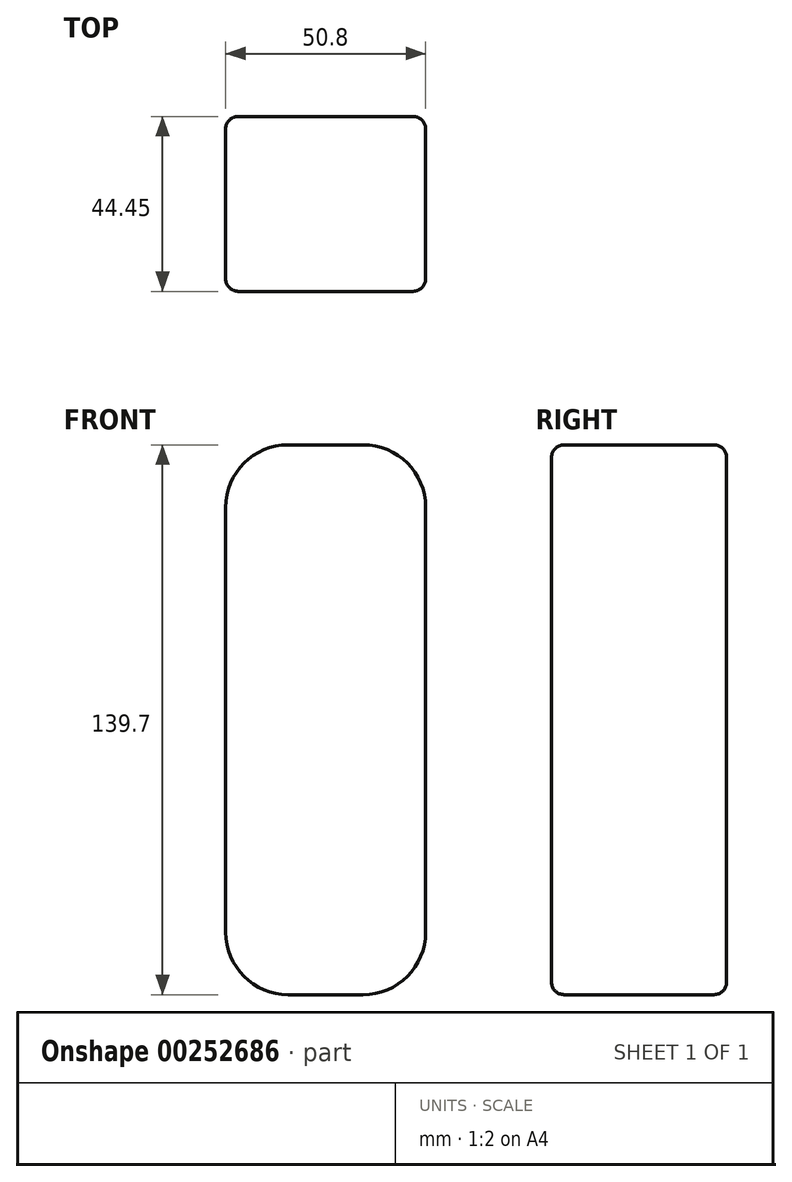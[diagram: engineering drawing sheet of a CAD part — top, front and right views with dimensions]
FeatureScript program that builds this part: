
annotation { "Feature Type Name" : "Feature", "Feature Type Description" : "" }
export const myFeature = defineFeature(function(context is Context, id is Id, definition is map)
    precondition{}
    {
        {
            var Q0;
            Q0=qCreatedBy(makeId("Front.planeOp"),FACE);
            var sketch = newSketch(context, id + "F0", { "sketchPlane" : qUnion([Q0])});
            skLineSegment(sketch, "E0.bottom", {"start": v(9.53, 69.85) * mm, "end": v(-9.53, 69.85) * mm});
            skLineSegment(sketch, "E0.top", {"start": v(9.52, -69.85) * mm, "end": v(-9.53, -69.85) * mm});
            skLineSegment(sketch, "E0.left", {"start": v(25.4, 53.98) * mm, "end": v(25.4, -53.98) * mm});
            skLineSegment(sketch, "E0.right", {"start": v(-25.4, 53.98) * mm, "end": v(-25.4, -53.98) * mm});
            skPoint(sketch, "E0.middle", {"position": v(0, 0) * mm});
            skPoint(sketch, "E1.visualSharp", {"position": v(-25.4, 69.85) * mm});
            skArc(sketch, "E1.filletArc", {"start": v(-9.53, 69.85) * mm, "mid": v(-20.75, 65.2) * mm, "end": v(-25.4, 53.98) * mm});
            skPoint(sketch, "E2.visualSharp", {"position": v(25.4, 69.85) * mm});
            skArc(sketch, "E2.filletArc", {"start": v(25.4, 53.98) * mm, "mid": v(20.75, 65.2) * mm, "end": v(9.53, 69.85) * mm});
            skPoint(sketch, "E3.visualSharp", {"position": v(25.4, -69.85) * mm});
            skArc(sketch, "E3.filletArc", {"start": v(9.53, -69.85) * mm, "mid": v(20.75, -65.2) * mm, "end": v(25.4, -53.98) * mm});
            skPoint(sketch, "E4.visualSharp", {"position": v(-25.4, -69.85) * mm});
            skArc(sketch, "E4.filletArc", {"start": v(-25.4, -53.98) * mm, "mid": v(-20.75, -65.2) * mm, "end": v(-9.53, -69.85) * mm});
            skSolve(sketch);
        }
        {
            var Q0;
            Q0 = qSketchRegion(id + "F0", true);
            extrude(context, id + "F1", {"entities" : qUnion([Q0]), "depth" : 44.45 * mm});
        }
        {
            var Q0;
            Q0=makeQuery(id+"F1.opExtrude","CAP_EDGE",EDGE,{"disambiguationData":[OSD([sQuery(id+"F0.wireOp",EDGE,"E2.filletArc")])],"isStart":false});
            var Q1;
            Q1=makeQuery(id+"F1.opExtrude","CAP_EDGE",EDGE,{"disambiguationData":[OSD([sQuery(id+"F0.wireOp",EDGE,"E0.bottom")])],"isStart":false});
            var Q2;
            Q2=makeQuery(id+"F1.opExtrude","CAP_EDGE",EDGE,{"disambiguationData":[OSD([sQuery(id+"F0.wireOp",EDGE,"E1.filletArc")])],"isStart":false});
            var Q3;
            Q3=makeQuery(id+"F1.opExtrude","CAP_EDGE",EDGE,{"disambiguationData":[OSD([sQuery(id+"F0.wireOp",EDGE,"E0.left")])],"isStart":false});
            var Q4;
            Q4=makeQuery(id+"F1.opExtrude","CAP_EDGE",EDGE,{"disambiguationData":[OSD([sQuery(id+"F0.wireOp",EDGE,"E3.filletArc")])],"isStart":false});
            var Q5;
            Q5=makeQuery(id+"F1.opExtrude","CAP_EDGE",EDGE,{"disambiguationData":[OSD([sQuery(id+"F0.wireOp",EDGE,"E0.top")])],"isStart":false});
            var Q6;
            Q6=makeQuery(id+"F1.opExtrude","CAP_EDGE",EDGE,{"disambiguationData":[OSD([sQuery(id+"F0.wireOp",EDGE,"E4.filletArc")])],"isStart":false});
            var Q7;
            Q7=makeQuery(id+"F1.opExtrude","CAP_EDGE",EDGE,{"disambiguationData":[OSD([sQuery(id+"F0.wireOp",EDGE,"E0.right")])],"isStart":false});
            var Q8;
            Q8=makeQuery(id+"F1.opExtrude","CAP_EDGE",EDGE,{"disambiguationData":[OSD([sQuery(id+"F0.wireOp",EDGE,"E2.filletArc")])],"isStart":true});
            var Q9;
            Q9=makeQuery(id+"F1.opExtrude","CAP_EDGE",EDGE,{"disambiguationData":[OSD([sQuery(id+"F0.wireOp",EDGE,"E0.left")])],"isStart":true});
            var Q10;
            Q10=makeQuery(id+"F1.opExtrude","CAP_EDGE",EDGE,{"disambiguationData":[OSD([sQuery(id+"F0.wireOp",EDGE,"E3.filletArc")])],"isStart":true});
            var Q11;
            Q11=makeQuery(id+"F1.opExtrude","CAP_EDGE",EDGE,{"disambiguationData":[OSD([sQuery(id+"F0.wireOp",EDGE,"E0.bottom")])],"isStart":true});
            var Q12;
            Q12=makeQuery(id+"F1.opExtrude","CAP_EDGE",EDGE,{"disambiguationData":[OSD([sQuery(id+"F0.wireOp",EDGE,"E1.filletArc")])],"isStart":true});
            var Q13;
            Q13=makeQuery(id+"F1.opExtrude","CAP_EDGE",EDGE,{"disambiguationData":[OSD([sQuery(id+"F0.wireOp",EDGE,"E0.top")])],"isStart":true});
            var Q14;
            Q14=makeQuery(id+"F1.opExtrude","CAP_EDGE",EDGE,{"disambiguationData":[OSD([sQuery(id+"F0.wireOp",EDGE,"E4.filletArc")])],"isStart":true});
            var Q15;
            Q15=makeQuery(id+"F1.opExtrude","CAP_EDGE",EDGE,{"disambiguationData":[OSD([sQuery(id+"F0.wireOp",EDGE,"E0.right")])],"isStart":true});
            fillet(context, id + "F2", {"entities" : qUnion([Q0, Q1, Q2, Q3, Q4, Q5, Q6, Q7, Q8, Q9, Q10, Q11, Q12, Q13, Q14, Q15]), "radius" : 3.17 * mm, "tangentPropagation" : true, "allowEdgeOverflow" : false});
        }
    });
